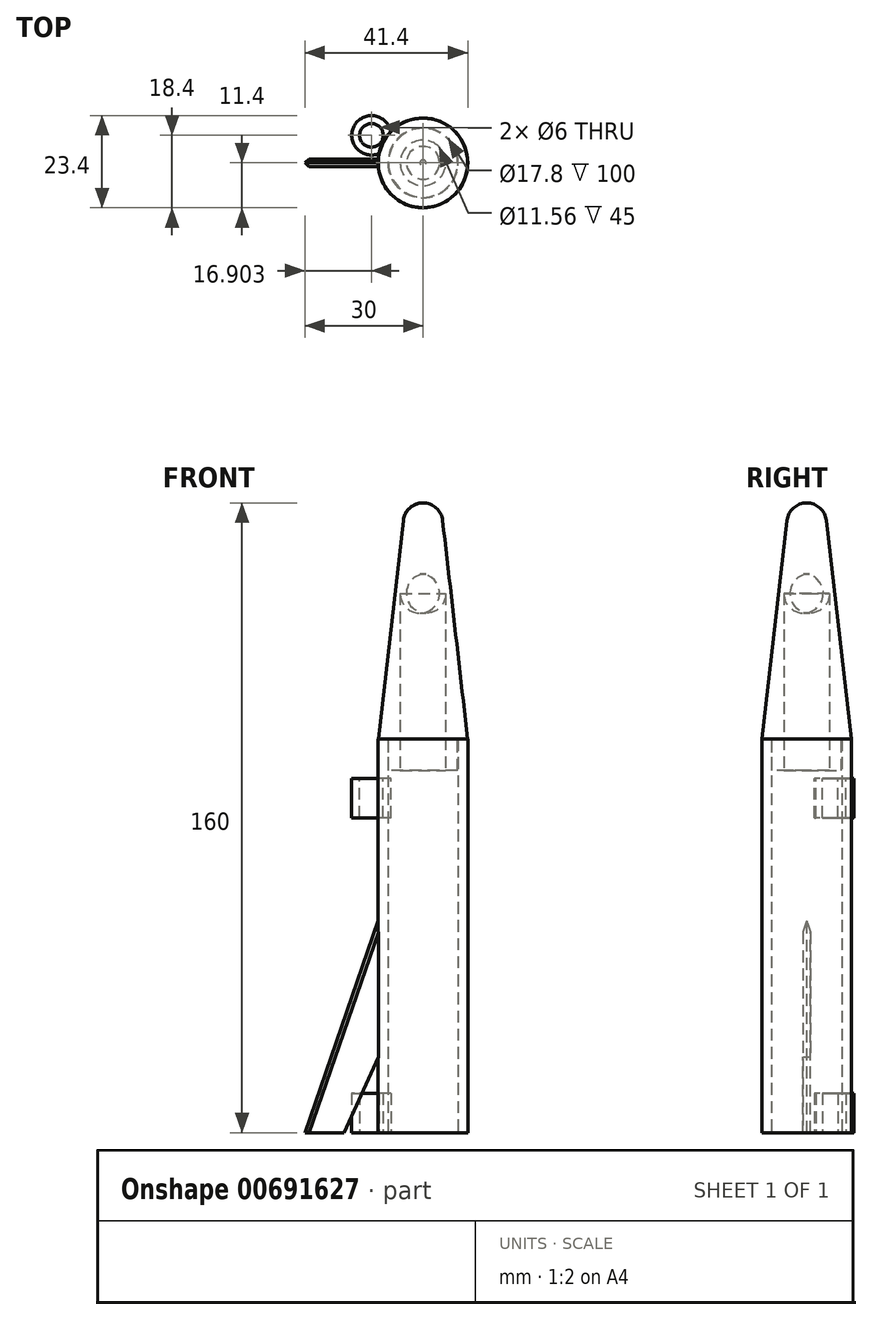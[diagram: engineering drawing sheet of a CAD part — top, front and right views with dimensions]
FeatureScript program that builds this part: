
annotation { "Feature Type Name" : "Feature", "Feature Type Description" : "" }
export const myFeature = defineFeature(function(context is Context, id is Id, definition is map)
    precondition{}
    {
        {
            var Q0;
            Q0=qCreatedBy(makeId("Top.planeOp"),FACE);
            var sketch = newSketch(context, id + "F0", { "sketchPlane" : qUnion([Q0])});
            skCircle(sketch, "E0", {"center": v(0, 0) * mm, "radius": 8.9 * mm});
            skCircle(sketch, "E1.0", {"center": v(0, 0) * mm, "radius": 11.4 * mm});
            skSolve(sketch);
        }
        {
            var Q0;
            Q0=makeQuery(id+"F0.imprint","IMPRINT",FACE,{"disambiguationData":[TD([[makeQuery(id+"F0.imprint","IMPRINT",EDGE,{"derivedFrom":sQuery(id+"F0.wireOp",EDGE,"E0")}),-1.0]])]});
            extrude(context, id + "F1", {"entities" : qUnion([Q0]), "depth" : 70 * mm, "offsetDistance" : 25 * mm});
        }
        {
            var Q0;
            Q0=makeQuery(id+"F1.opExtrude","CAP_FACE",FACE,{"disambiguationData":[OSD([sQuery(id+"F0.wireOp",EDGE,"E0"),sQuery(id+"F0.wireOp",EDGE,"E1.0")])],"isStart":false});
            var sketch = newSketch(context, id + "F2", { "sketchPlane" : qUnion([Q0])});
            skCircle(sketch, "E2.0", {"center": v(0, 0) * mm, "radius": 11.4 * mm});
            skCircle(sketch, "E3.0", {"center": v(0, 0) * mm, "radius": 8.78 * mm});
            skSolve(sketch);
        }
        {
            var Q0;
            Q0=makeQuery(id+"F1.opExtrude","CAP_FACE",FACE,{"disambiguationData":[OSD([sQuery(id+"F0.wireOp",EDGE,"E0"),sQuery(id+"F0.wireOp",EDGE,"E1.0")])],"isStart":false});
            var sketch = newSketch(context, id + "F3", { "sketchPlane" : qUnion([Q0])});
            skCircle(sketch, "E4", {"center": v(0, 0) * mm, "radius": 11.35 * mm});
            skSolve(sketch);
        }
        {
            var Q0;
            Q0=qCreatedBy(makeId("Front.planeOp"),FACE);
            var sketch = newSketch(context, id + "F4", { "sketchPlane" : qUnion([Q0])});
            skLineSegment(sketch, "E5", {"start": v(-11.35, 100) * mm, "end": v(-5, 155.54) * mm});
            skLineSegment(sketch, "E6", {"start": v(0, 0) * mm, "end": v(0, 404.97) * mm, "construction": true});
            skLineSegment(sketch, "E7", {"start": v(-5, 155.54) * mm, "end": v(0, 155.54) * mm, "construction": true});
            skLineSegment(sketch, "E8", {"start": v(0, 155.54) * mm, "end": v(5, 155.54) * mm, "construction": true});
            skArc(sketch, "E9", {"start": v(5, 155.54) * mm, "mid": v(0, 160) * mm, "end": v(-5, 155.54) * mm});
            skLineSegment(sketch, "E10", {"start": v(0, 160) * mm, "end": v(0, 100) * mm});
            skLineSegment(sketch, "E11", {"start": v(0, 100) * mm, "end": v(-11.35, 100) * mm});
            skSolve(sketch);
        }
        {
            var Q0;
            {var subQ0=sQuery(id+"F4.wireOp",EDGE,"E5");Q0=makeQuery(id+"F4.imprint","IMPRINT",FACE,{"disambiguationData":[TD([[makeQuery(id+"F4.imprint","IMPRINT",EDGE,{"derivedFrom":subQ0}),-1.0]])]});}
            var Q1;
            Q1=sQuery(id+"F4.wireOp",EDGE,"E10");
            revolve(context, id + "F5", {"entities" : qUnion([Q0]), "axis" : qUnion([Q1]), "revolveType" : RevolveType.FULL});
        }
        {
            var Q0;
            Q0=qCreatedBy(makeId("Front.planeOp"),FACE);
            var sketch = newSketch(context, id + "F6", { "sketchPlane" : qUnion([Q0])});
            skLineSegment(sketch, "E12", {"start": v(-20, 0) * mm, "end": v(-11, 20) * mm});
            skLineSegment(sketch, "E13", {"start": v(-11, 20) * mm, "end": v(-11, 55) * mm});
            skLineSegment(sketch, "E14", {"start": v(-11, 55) * mm, "end": v(-30, 0) * mm});
            skLineSegment(sketch, "E15", {"start": v(-30, 0) * mm, "end": v(-20, 0) * mm});
            skSolve(sketch);
        }
        {
            var Q0;
            Q0=makeQuery(id+"F6.imprint","IMPRINT",FACE,{"disambiguationData":[TD([[makeQuery(id+"F6.imprint","IMPRINT",EDGE,{"derivedFrom":sQuery(id+"F6.wireOp",EDGE,"E12")}),1.0]])]});
            extrude(context, id + "F7", {"entities" : qUnion([Q0]), "operationType" : NewBodyOperationType.ADD, "endBound" : BoundingType.SYMMETRIC, "depth" : 2 * mm, "offsetDistance" : 25 * mm});
        }
        {
            var Q0;
            Q0=makeQuery(id+"F7.opExtrude","CAP_EDGE",EDGE,{"disambiguationData":[OSD([sQuery(id+"F6.wireOp",EDGE,"E14")])],"isStart":false});
            var Q1;
            Q1=makeQuery(id+"F7.opExtrude","CAP_EDGE",EDGE,{"disambiguationData":[OSD([sQuery(id+"F6.wireOp",EDGE,"E14")])],"isStart":true});
            chamfer(context, id + "F8", {"entities" : qUnion([Q0, Q1]), "width" : 1 * mm, "tangentPropagation" : true});
        }
        {
            var Q0;
            Q0=makeQuery(id+"F2.imprint","IMPRINT",FACE,{"disambiguationData":[TD([[makeQuery(id+"F2.imprint","IMPRINT",EDGE,{"derivedFrom":sQuery(id+"F2.wireOp",EDGE,"E2.0")}),1.0]])]});
            extrude(context, id + "F9", {"entities" : qUnion([Q0]), "operationType" : NewBodyOperationType.ADD, "depth" : 30 * mm, "offsetDistance" : 25 * mm});
        }
        {
            var Q0;
            Q0=makeQuery(id+"F5.opRevolve","SWEPT_FACE",FACE,{"disambiguationData":[OSD([sQuery(id+"F4.wireOp",EDGE,"E11")])]});
            var sketch = newSketch(context, id + "F10", { "sketchPlane" : qUnion([Q0])});
            skCircle(sketch, "E16.0", {"center": v(0, 0) * mm, "radius": 8.78 * mm});
            skSolve(sketch);
        }
        {
            var Q0;
            Q0=makeQuery(id+"F10.imprint","IMPRINT",FACE,{"disambiguationData":[TD([[makeQuery(id+"F10.imprint","IMPRINT",EDGE,{"derivedFrom":sQuery(id+"F10.wireOp",EDGE,"E16.0")}),1.0]])]});
            extrude(context, id + "F11", {"entities" : qUnion([Q0]), "operationType" : NewBodyOperationType.ADD, "depth" : 8 * mm, "offsetDistance" : 25 * mm});
        }
        {
            var Q0;
            Q0=qCreatedBy(makeId("Top.planeOp"),FACE);
            cPlane(context, id + "F12", {"entities" : qUnion([Q0]), "cplaneType" : CPlaneType.OFFSET, "offset" : 90 * mm, "width" : 150 * mm, "height" : 150 * mm});
        }
        {
            var Q0;
            Q0=qCreatedBy(id+"F12.planeOp",FACE);
            var sketch = newSketch(context, id + "F13", { "sketchPlane" : qUnion([Q0])});
            skCircle(sketch, "E17", {"center": v(-13.1, 7) * mm, "radius": 3 * mm});
            skCircle(sketch, "E18.0", {"center": v(-13.1, 7) * mm, "radius": 5 * mm});
            skSolve(sketch);
        }
        {
            var Q0;
            Q0=makeQuery(id+"F13.imprint","IMPRINT",FACE,{"disambiguationData":[TD([[makeQuery(id+"F13.imprint","IMPRINT",EDGE,{"derivedFrom":sQuery(id+"F13.wireOp",EDGE,"E17")}),-1.0]])]});
            extrude(context, id + "F14", {"entities" : qUnion([Q0]), "operationType" : NewBodyOperationType.ADD, "oppositeDirection" : true, "depth" : 10 * mm, "offsetDistance" : 25 * mm});
        }
        {
            var Q0;
            Q0=qCreatedBy(makeId("Top.planeOp"),FACE);
            var sketch = newSketch(context, id + "F15", { "sketchPlane" : qUnion([Q0])});
            skCircle(sketch, "E19", {"center": v(-13.1, 7) * mm, "radius": 3 * mm});
            skCircle(sketch, "E20.0", {"center": v(-13.1, 7) * mm, "radius": 5 * mm});
            skSolve(sketch);
        }
        {
            var Q0;
            Q0=makeQuery(id+"F15.imprint","IMPRINT",FACE,{"disambiguationData":[TD([[makeQuery(id+"F15.imprint","IMPRINT",EDGE,{"derivedFrom":sQuery(id+"F15.wireOp",EDGE,"E19")}),-1.0]])]});
            extrude(context, id + "F16", {"entities" : qUnion([Q0]), "operationType" : NewBodyOperationType.ADD, "depth" : 10 * mm, "offsetDistance" : 25 * mm});
        }
        {
            var Q0;
            Q0=makeQuery(id+"F11.opExtrude","CAP_FACE",FACE,{"disambiguationData":[OSD([sQuery(id+"F10.wireOp",EDGE,"E16.0")])],"isStart":false});
            var sketch = newSketch(context, id + "F17", { "sketchPlane" : qUnion([Q0])});
            skCircle(sketch, "E21.0", {"center": v(0, 0) * mm, "radius": 5.78 * mm});
            skSolve(sketch);
        }
        {
            var Q0;
            Q0=makeQuery(id+"F17.imprint","IMPRINT",FACE,{"disambiguationData":[TD([[makeQuery(id+"F17.imprint","IMPRINT",EDGE,{"derivedFrom":sQuery(id+"F17.wireOp",EDGE,"E21.0")}),1.0]])]});
            extrude(context, id + "F18", {"entities" : qUnion([Q0]), "operationType" : NewBodyOperationType.REMOVE, "oppositeDirection" : true, "depth" : 50 * mm, "offsetDistance" : 25 * mm});
        }
        {
            var Q0;
            Q0=makeQuery(id+"F18.boolean.opBoolean","COPY",EDGE,{"derivedFrom":makeQuery(id+"F18.opExtrude","CAP_EDGE",EDGE,{"disambiguationData":[OSD([sQuery(id+"F17.wireOp",EDGE,"E21.0")])],"isStart":false})});
            fillet(context, id + "F19", {"entities" : qUnion([Q0]), "radius" : 5 * mm, "tangentPropagation" : true, "allowEdgeOverflow" : false});
        }
    });
